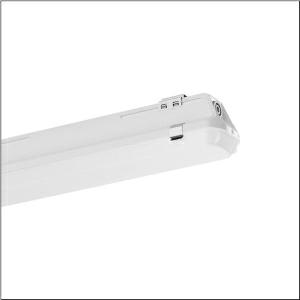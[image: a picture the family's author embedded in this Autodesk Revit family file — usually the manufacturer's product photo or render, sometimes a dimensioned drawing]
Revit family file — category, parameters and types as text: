
# Revit family: monsun_r__21_51fb207l440j_6c80
name_source: partatom
category: Lighting Fixtures
units: mm (PartAtom-declared; Revit-internal decimal feet)

## family parameters
Cut with Voids When Loaded = No
Host = Face
Light Source = No
Part Type = Normal
Room Calculation Point = No
Round Connector Dimension = Use Diameter
Shared = No

## types (1)
- Monsun® 21 (1 x LED, 4410 lm, 29.8 W, 4000K)
    Apparent Load = 30 VA
    CIE Flux Codes = 45 75 93 94 100
    Color Rendering = 80
    Color Temperature = 4000K
    Default Elevation = 1800 mm
    Description = Monsun® 21, damp-proof luminaire, chain hanger, primary optical cover: enclosure, of PC, light emission: direct distribution, primary light characteristic: symmetric, installation type: suspended mounting, surface-mounted, horizontal mounting, vertical mounting, LED, rated luminous flux: 4.410lm, luminous efficacy: 147lm/W, light colour: 840, colour temperature: 4000K, control gear: ECG, with terminal, 3-pole, max. 2.5mm², mains connection: 220..240V, AC, 50/60Hz, rated input power: 30W, housing, of glass-fibre reinforced plastic, uncoated, bright grey, incl. chain hanger, length: 1.299mm, width: 90mm, height: 88mm, clip for enclosure, of stainless steel (V2A), ceiling mounting element, of stainless steel (V2A), chain hanger, of stainless steel (V2A), protection rating (complete): IP66, insulation class (complete): insulation class I (protective earthing), certification: CE, ENEC, VDE, UKCA, protection symbol: D, impact resistance: IK08, permissible operating ambient temperature: -25..+35°C, standard: EN 50419, EN 60598-2-1, no direct snow, no direct sun, no direct rain, for indoor or canopied outdoor use, corresponds to IFS (International Featured Standards) requirements for safety and quality in the food industry, contact your sales advisor before using the luminaires in applications with unclear chemical exposure, large temperature fluctuations or condensation-forming humidity, LABS conformity tested according to VDMA 24364:2018-05, packaging unit: 1 piece
    Height = 88 mm
    Lamp = 1 x LED
    Lamp Light Flux = 4410 lm
    Lamp Power = 29.8 W
    Lamp count = 1
    Length = 1299 mm
    Luminous efficacy = 148 lm/W
    Manufacturer = Siteco
    ModVariant = No
    Model = 51FB207L440J
    Mounting Place = Ceiling
    Mounting Type = Surface mounted
    Number of Poles = 1
    OnlyDefault = Yes
    Power Factor = 1
    Product Name = Monsun® 21
    Product group = damp-proof luminaire
    ProductGroupID = 300
    Protection Class = Protection class I
    Protection Degree = IP 66
    RLX_Detail_Level = 1
    RLX_Emergency_Light_Flux = 0 lm
    RLX_Emergency_Type = 0
    RLX_Emergency_Type_DB = No
    RlxData = <blob elided: 90117 chars, md5=915c881a>
    Socket = socket
    Standby Power = 0 W
    System Light Flux = 4410 lm
    System Power = 30 W
    Type Comments = Product without accessories
    Type Image = l_1006717.jpg
    URL = http://relux.com
    VarID = ---
    Voltage = 0 V
    Weight = 0.00 kg
    Width = 90 mm

## geometry (parser evidence)
native form markers: Blend x4, Sweep x12
no freeform markers — native parametric forms only
